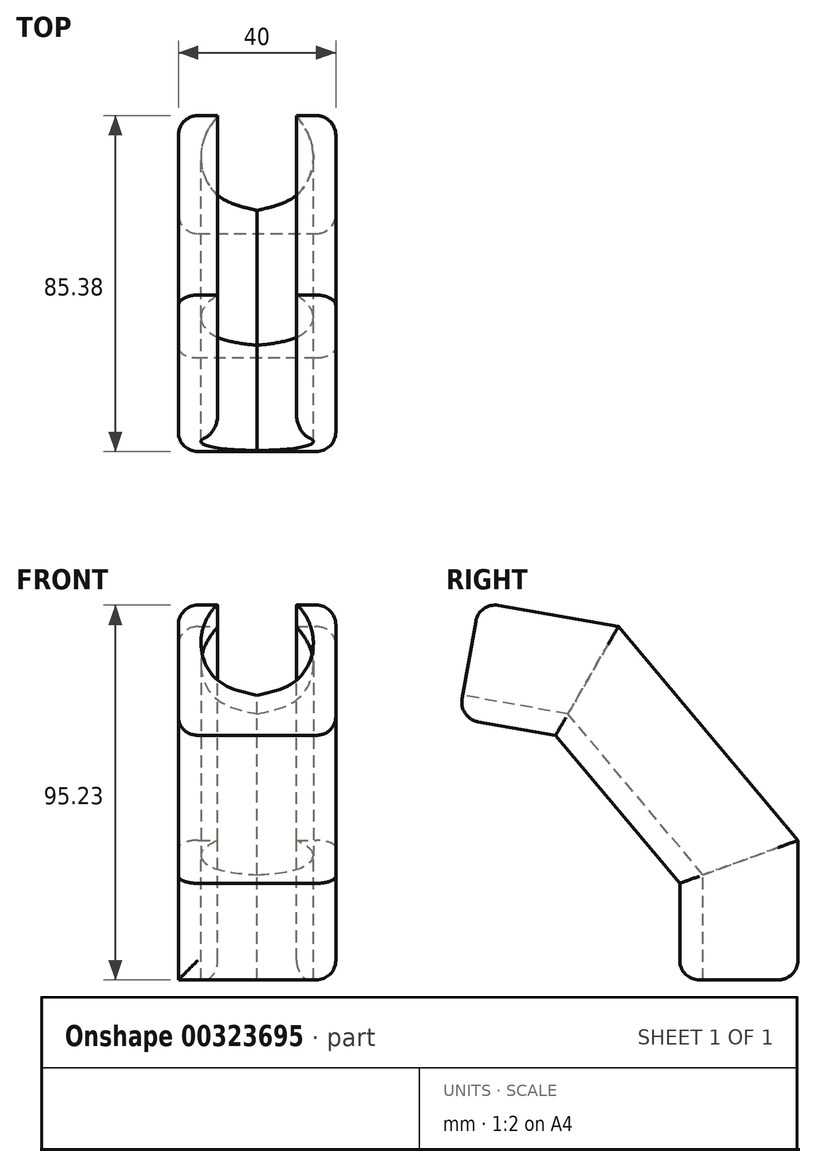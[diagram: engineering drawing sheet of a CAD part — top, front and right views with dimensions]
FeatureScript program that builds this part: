
annotation { "Feature Type Name" : "Feature", "Feature Type Description" : "" }
export const myFeature = defineFeature(function(context is Context, id is Id, definition is map)
    precondition{}
    {
        {
            var Q0;
            Q0=qCreatedBy(makeId("Top.planeOp"),FACE);
            var sketch = newSketch(context, id + "F0", { "sketchPlane" : qUnion([Q0])});
            skLineSegment(sketch, "E0.bottom", {"start": v(-20, 15) * mm, "end": v(-10, 15) * mm});
            skLineSegment(sketch, "E0.top", {"start": v(-20, -15) * mm, "end": v(20, -15) * mm});
            skLineSegment(sketch, "E0.left", {"start": v(-20, 15) * mm, "end": v(-20, -15) * mm});
            skLineSegment(sketch, "E0.right", {"start": v(20, 15) * mm, "end": v(20, -15) * mm});
            skPoint(sketch, "E0.middle", {"position": v(0, 0) * mm});
            skPoint(sketch, "E1", {"position": v(-10, 15) * mm});
            skPoint(sketch, "E2", {"position": v(10, 15) * mm});
            skPoint(sketch, "E3", {"position": v(124.4, 53.34) * mm});
            skFitSpline(sketch, "E4", {"points": [v(-10, 15) * mm, v(-13, 10.22) * mm, v(-14.2, 2.98) * mm, v(-10, -5.23) * mm, v(0, -9.09) * mm], "startDerivative": vector(-15.7, -21.33) * mm, "endDerivative": vector(38.65, -8.74) * mm});
            skPoint(sketch, "E5.endSnap0", {"position": v(0, 15) * mm});
            skFitSpline(sketch, "E6.MirrorCS", {"points": [v(10, 15) * mm, v(13, 10.22) * mm, v(14.2, 2.98) * mm, v(10, -5.23) * mm, v(0, -9.09) * mm], "startDerivative": vector(15.7, -21.33) * mm, "endDerivative": vector(-38.65, -8.74) * mm});
            skLineSegment(sketch, "E7.trimOffspring", {"start": v(10, 15) * mm, "end": v(20, 15) * mm});
            skPoint(sketch, "E5.end.orphan", {"position": v(0, 8.05) * mm});
            skPoint(sketch, "E5.start.orphan", {"position": v(0, 15) * mm});
            skSolve(sketch);
        }
        {
            var Q0;
            Q0=qCreatedBy(makeId("Right.planeOp"),FACE);
            var sketch = newSketch(context, id + "F1", { "sketchPlane" : qUnion([Q0])});
            skLineSegment(sketch, "E8", {"start": v(0, 0) * mm, "end": v(0, 30) * mm});
            skLineSegment(sketch, "E9", {"start": v(0, 30) * mm, "end": v(-38.57, 75.96) * mm});
            skLineSegment(sketch, "E10", {"start": v(-38.57, 75.96) * mm, "end": v(-68.57, 81.25) * mm});
            skSolve(sketch);
        }
        {
            var Q0;
            Q0 = qSketchRegion(id + "F0", true);
            var Q1;
            Q1 = qConstructionFilter(qBodyType(qCreatedBy(id + "F1" ,EDGE), BodyType.WIRE), ConstructionObject.NO);
            sweep(context, id + "F2", {"profiles" : qUnion([Q0]), "path" : qUnion([Q1])});
        }
        {
            var Q0;
            Q0=makeQuery(id+"F2.opSweep","SWEPT_EDGE",EDGE,{"disambiguationData":[OSD([sQuery(id+"F0.wireOp",EDGE,"E0.bottom"),sQuery(id+"F0.wireOp",EDGE,"E0.left"),sQuery(id+"F1.wireOp",EDGE,"E9")])]});
            var Q1;
            Q1=makeQuery(id+"F2.opSweep","SWEPT_EDGE",EDGE,{"disambiguationData":[OSD([sQuery(id+"F0.wireOp",EDGE,"E0.bottom"),sQuery(id+"F0.wireOp",EDGE,"E0.left"),sQuery(id+"F1.wireOp",EDGE,"E8")])]});
            var Q2;
            Q2=makeQuery(id+"F2.opSweep","SWEPT_EDGE",EDGE,{"disambiguationData":[OSD([sQuery(id+"F0.wireOp",EDGE,"E0.top"),sQuery(id+"F0.wireOp",EDGE,"E0.left"),sQuery(id+"F1.wireOp",EDGE,"E8")])]});
            var Q3;
            Q3=makeQuery(id+"F2.opSweep","SWEPT_EDGE",EDGE,{"disambiguationData":[OSD([sQuery(id+"F0.wireOp",EDGE,"E0.top"),sQuery(id+"F0.wireOp",EDGE,"E0.left"),sQuery(id+"F1.wireOp",EDGE,"E9")])]});
            var Q4;
            Q4=makeQuery(id+"F2.opSweep","SWEPT_EDGE",EDGE,{"disambiguationData":[OSD([sQuery(id+"F0.wireOp",EDGE,"E0.top"),sQuery(id+"F0.wireOp",EDGE,"E0.left"),sQuery(id+"F1.wireOp",EDGE,"E10")])]});
            var Q5;
            Q5=makeQuery(id+"F2.opSweep","CAP_EDGE",EDGE,{"disambiguationData":[OSD([sQuery(id+"F0.wireOp",EDGE,"E0.left"),sQuery(id+"F1.wireOp",VERTEX,"E10.end")])],"isStart":false});
            var Q6;
            Q6=makeQuery(id+"F2.opSweep","SWEPT_EDGE",EDGE,{"disambiguationData":[OSD([sQuery(id+"F0.wireOp",EDGE,"E0.bottom"),sQuery(id+"F0.wireOp",EDGE,"E0.left"),sQuery(id+"F1.wireOp",EDGE,"E10")])]});
            var Q7;
            Q7=makeQuery(id+"F2.opSweep","SWEPT_EDGE",EDGE,{"disambiguationData":[OSD([sQuery(id+"F0.wireOp",EDGE,"E0.right"),sQuery(id+"F0.wireOp",EDGE,"E7.trimOffspring"),sQuery(id+"F1.wireOp",EDGE,"E9")])]});
            var Q8;
            Q8=makeQuery(id+"F2.opSweep","SWEPT_EDGE",EDGE,{"disambiguationData":[OSD([sQuery(id+"F0.wireOp",EDGE,"E0.right"),sQuery(id+"F0.wireOp",EDGE,"E7.trimOffspring"),sQuery(id+"F1.wireOp",EDGE,"E8")])]});
            var Q9;
            Q9=makeQuery(id+"F2.opSweep","SWEPT_EDGE",EDGE,{"disambiguationData":[OSD([sQuery(id+"F0.wireOp",EDGE,"E0.right"),sQuery(id+"F0.wireOp",EDGE,"E7.trimOffspring"),sQuery(id+"F1.wireOp",EDGE,"E10")])]});
            var Q10;
            Q10=makeQuery(id+"F2.opSweep","CAP_EDGE",EDGE,{"disambiguationData":[OSD([sQuery(id+"F0.wireOp",EDGE,"E0.right"),sQuery(id+"F1.wireOp",VERTEX,"E8.start")])],"isStart":true});
            var Q11;
            Q11=makeQuery(id+"F2.opSweep","SWEPT_EDGE",EDGE,{"disambiguationData":[OSD([sQuery(id+"F0.wireOp",EDGE,"E0.top"),sQuery(id+"F0.wireOp",EDGE,"E0.right"),sQuery(id+"F1.wireOp",EDGE,"E8")])]});
            var Q12;
            Q12=makeQuery(id+"F2.opSweep","SWEPT_EDGE",EDGE,{"disambiguationData":[OSD([sQuery(id+"F0.wireOp",EDGE,"E0.top"),sQuery(id+"F0.wireOp",EDGE,"E0.right"),sQuery(id+"F1.wireOp",EDGE,"E9")])]});
            var Q13;
            Q13=makeQuery(id+"F2.opSweep","SWEPT_EDGE",EDGE,{"disambiguationData":[OSD([sQuery(id+"F0.wireOp",EDGE,"E0.top"),sQuery(id+"F0.wireOp",EDGE,"E0.right"),sQuery(id+"F1.wireOp",EDGE,"E10")])]});
            var Q14;
            Q14=makeQuery(id+"F2.opSweep","CAP_EDGE",EDGE,{"disambiguationData":[OSD([sQuery(id+"F0.wireOp",EDGE,"E0.right"),sQuery(id+"F1.wireOp",VERTEX,"E10.end")])],"isStart":false});
            var Q15;
            Q15=makeQuery(id+"F2.opSweep","CAP_EDGE",EDGE,{"disambiguationData":[OSD([sQuery(id+"F0.wireOp",EDGE,"E7.trimOffspring"),sQuery(id+"F1.wireOp",VERTEX,"E10.end")])],"isStart":false});
            var Q16;
            Q16=makeQuery(id+"F2.opSweep","CAP_EDGE",EDGE,{"disambiguationData":[OSD([sQuery(id+"F0.wireOp",EDGE,"E0.bottom"),sQuery(id+"F1.wireOp",VERTEX,"E10.end")])],"isStart":false});
            var Q17;
            Q17=makeQuery(id+"F2.opSweep","CAP_EDGE",EDGE,{"disambiguationData":[OSD([sQuery(id+"F0.wireOp",EDGE,"E0.top"),sQuery(id+"F1.wireOp",VERTEX,"E10.end")])],"isStart":false});
            var Q18;
            Q18=makeQuery(id+"F2.opSweep","CAP_EDGE",EDGE,{"disambiguationData":[OSD([sQuery(id+"F0.wireOp",EDGE,"E0.top"),sQuery(id+"F1.wireOp",VERTEX,"E8.start")])],"isStart":true});
            var Q19;
            Q19=makeQuery(id+"F2.opSweep","CAP_EDGE",EDGE,{"disambiguationData":[OSD([sQuery(id+"F0.wireOp",EDGE,"E0.bottom"),sQuery(id+"F1.wireOp",VERTEX,"E8.start")])],"isStart":true});
            var Q20;
            Q20=makeQuery(id+"F2.opSweep","CAP_EDGE",EDGE,{"disambiguationData":[OSD([sQuery(id+"F0.wireOp",EDGE,"E7.trimOffspring"),sQuery(id+"F1.wireOp",VERTEX,"E8.start")])],"isStart":true});
            fillet(context, id + "F3", {"entities" : qUnion([Q0, Q1, Q2, Q3, Q4, Q5, Q6, Q7, Q8, Q9, Q10, Q11, Q12, Q13, Q14, Q15, Q16, Q17, Q18, Q19, Q20]), "radius" : 5 * mm, "tangentPropagation" : true, "allowEdgeOverflow" : false});
        }
    });
